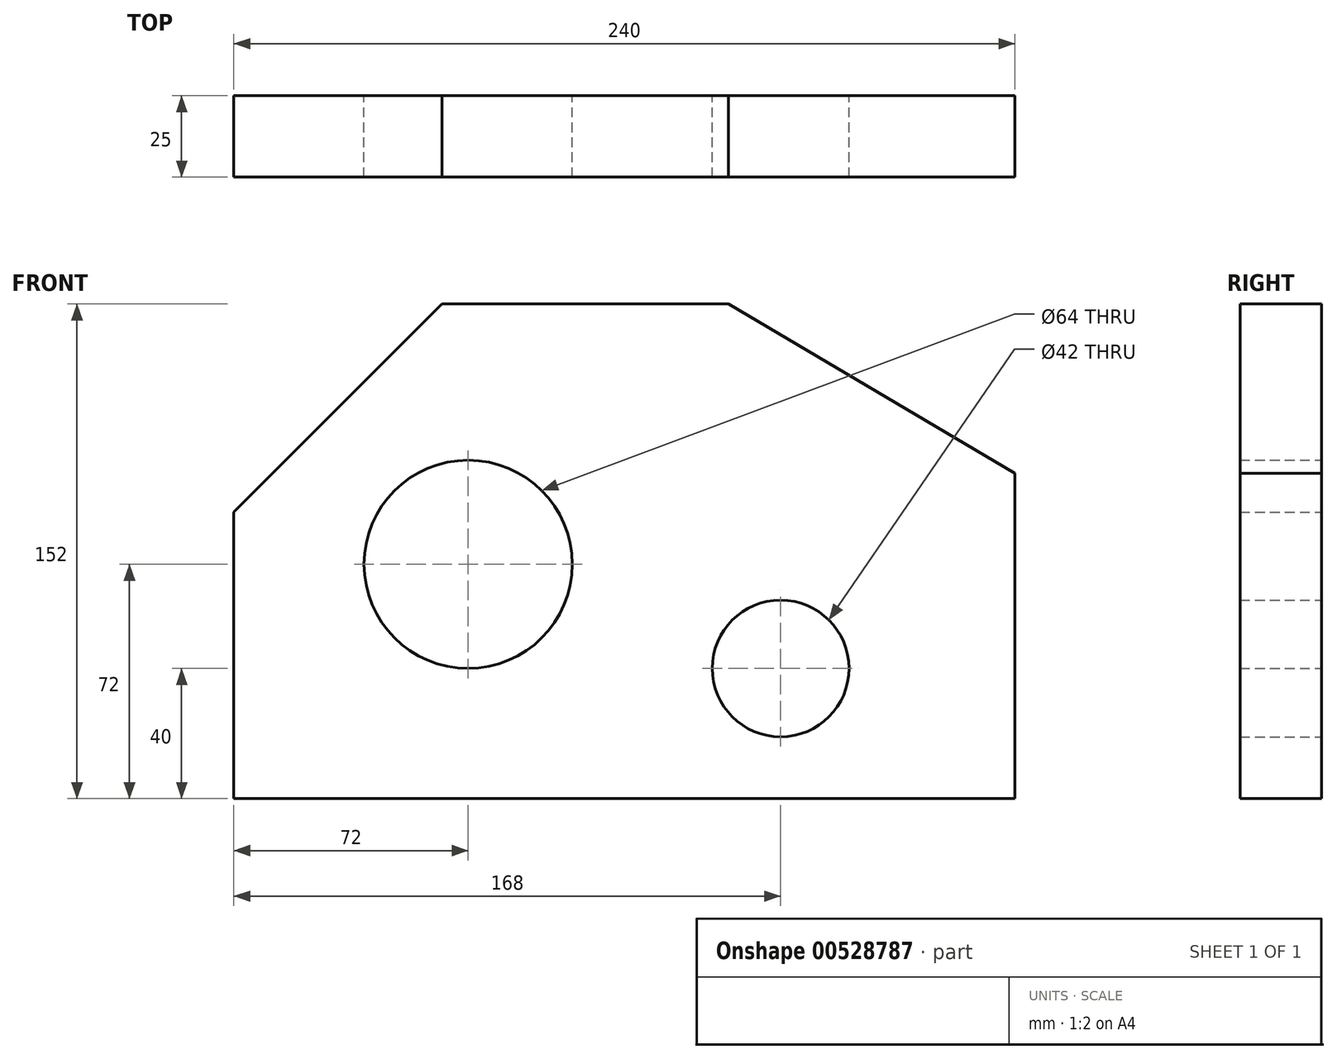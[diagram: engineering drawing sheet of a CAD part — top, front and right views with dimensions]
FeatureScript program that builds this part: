
annotation { "Feature Type Name" : "Feature", "Feature Type Description" : "" }
export const myFeature = defineFeature(function(context is Context, id is Id, definition is map)
    precondition{}
    {
        {
            var Q0;
            Q0=qCreatedBy(makeId("Front.planeOp"),FACE);
            var sketch = newSketch(context, id + "F0", { "sketchPlane" : qUnion([Q0])});
            skLineSegment(sketch, "E0", {"start": v(0, 0) * mm, "end": v(0, 88) * mm});
            skLineSegment(sketch, "E1", {"start": v(0, 88) * mm, "end": v(64, 152) * mm});
            skLineSegment(sketch, "E2", {"start": v(64, 152) * mm, "end": v(152, 152) * mm});
            skLineSegment(sketch, "E3", {"start": v(152, 152) * mm, "end": v(240, 100) * mm});
            skLineSegment(sketch, "E4", {"start": v(240, 100) * mm, "end": v(240, 0) * mm});
            skLineSegment(sketch, "E5", {"start": v(240, 0) * mm, "end": v(0, 0) * mm});
            skCircle(sketch, "E6", {"center": v(72, 72) * mm, "radius": 32 * mm});
            skCircle(sketch, "E7", {"center": v(168, 40) * mm, "radius": 21 * mm});
            skLineSegment(sketch, "E8", {"start": v(168, 40) * mm, "end": v(168, 142.55) * mm, "construction": true});
            skSolve(sketch);
        }
        {
            var Q0;
            Q0 = qSketchRegion(id + "F0", true);
            extrude(context, id + "F1", {"entities" : qUnion([Q0]), "depth" : 25 * mm, "offsetDistance" : 25 * mm});
        }
    });
